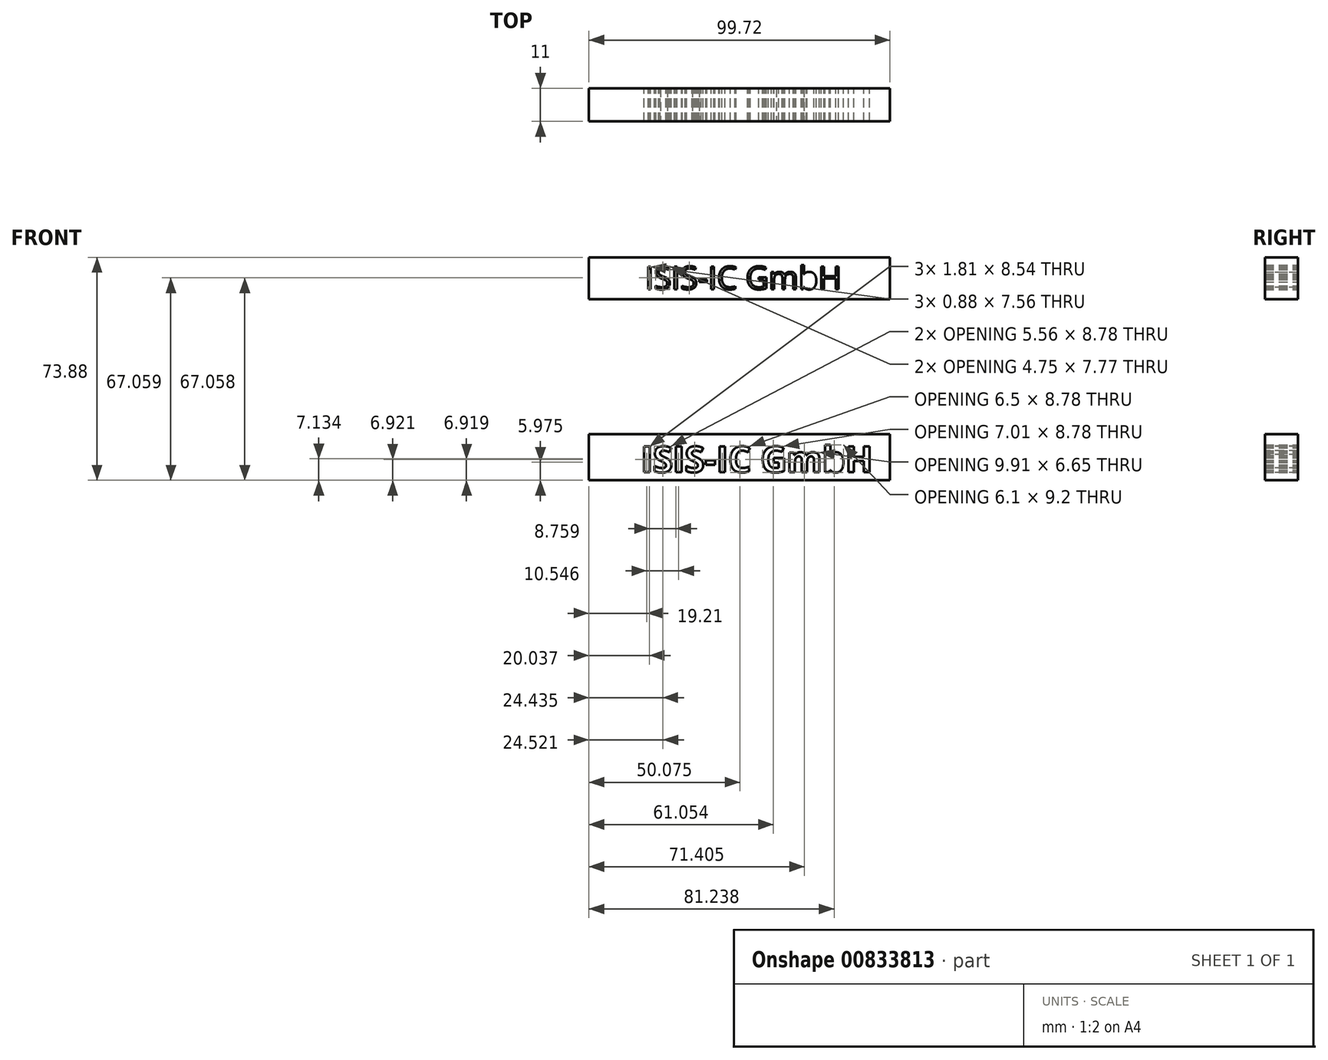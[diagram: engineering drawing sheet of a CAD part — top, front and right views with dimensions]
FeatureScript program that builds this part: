
annotation { "Feature Type Name" : "Feature", "Feature Type Description" : "" }
export const myFeature = defineFeature(function(context is Context, id is Id, definition is map)
    precondition{}
    {
        {
            var Q0;
            Q0=qCreatedBy(makeId("Front.planeOp"),FACE);
            var sketch = newSketch(context, id + "F0", { "sketchPlane" : qUnion([Q0])});
            skLineSegment(sketch, "E0.bottom", {"start": v(49.86, 30.15) * mm, "end": v(-49.86, 30.15) * mm});
            skLineSegment(sketch, "E0.top", {"start": v(49.86, 44.06) * mm, "end": v(-49.86, 44.06) * mm});
            skLineSegment(sketch, "E0.left", {"start": v(49.86, 30.15) * mm, "end": v(49.86, 44.06) * mm});
            skLineSegment(sketch, "E0.right", {"start": v(-49.86, 30.15) * mm, "end": v(-49.86, 44.06) * mm});
            skPoint(sketch, "E0.middle", {"position": v(0, 37.1) * mm});
            skText(sketch, "E1", { "text": "ISIS-IC GmbH", "fontName": "OpenSans-Regular.ttf"});
            skLineSegment(sketch, "E2.bottom", {"start": v(49.86, -29.82) * mm, "end": v(-49.86, -29.82) * mm});
            skLineSegment(sketch, "E2.top", {"start": v(49.86, -14.58) * mm, "end": v(-49.86, -14.58) * mm});
            skLineSegment(sketch, "E2.left", {"start": v(49.86, -29.82) * mm, "end": v(49.86, -14.58) * mm});
            skLineSegment(sketch, "E2.right", {"start": v(-49.86, -29.82) * mm, "end": v(-49.86, -14.58) * mm});
            skPoint(sketch, "E2.middle", {"position": v(0, -22.2) * mm});
            skText(sketch, "E3", { "text": "ISIS-IC GmbH", "fontName": "OpenSans-Bold.ttf"});
            const initialGuessF0  = {"E1": [-0.0313, 0.03346, 1, 0, 0.00762], "E3": [-0.03263, -0.02717, 1, 0, 0.00861]};
            skSetInitialGuess(sketch, initialGuessF0);
            skSolve(sketch);
        }
        {
            var Q0;
            Q0=makeQuery(id+"F0.imprint","IMPRINT",FACE,{"disambiguationData":[TD([[makeQuery(id+"F0.imprint","IMPRINT",EDGE,{"derivedFrom":sQuery(id+"F0.wireOp",EDGE,"E0.bottom")}),-1.0]])]});
            extrude(context, id + "F1", {"entities" : qUnion([Q0]), "depth" : 11 * mm, "offsetDistance" : 25 * mm});
        }
        {
            var Q0;
            Q0=makeQuery(id+"F0.imprint","IMPRINT",FACE,{"disambiguationData":[TD([[makeQuery(id+"F0.imprint","IMPRINT",EDGE,{"derivedFrom":sQuery(id+"F0.wireOp",EDGE,"E2.bottom")}),-1.0]])]});
            extrude(context, id + "F2", {"entities" : qUnion([Q0]), "depth" : 11 * mm, "offsetDistance" : 25 * mm});
        }
    });
